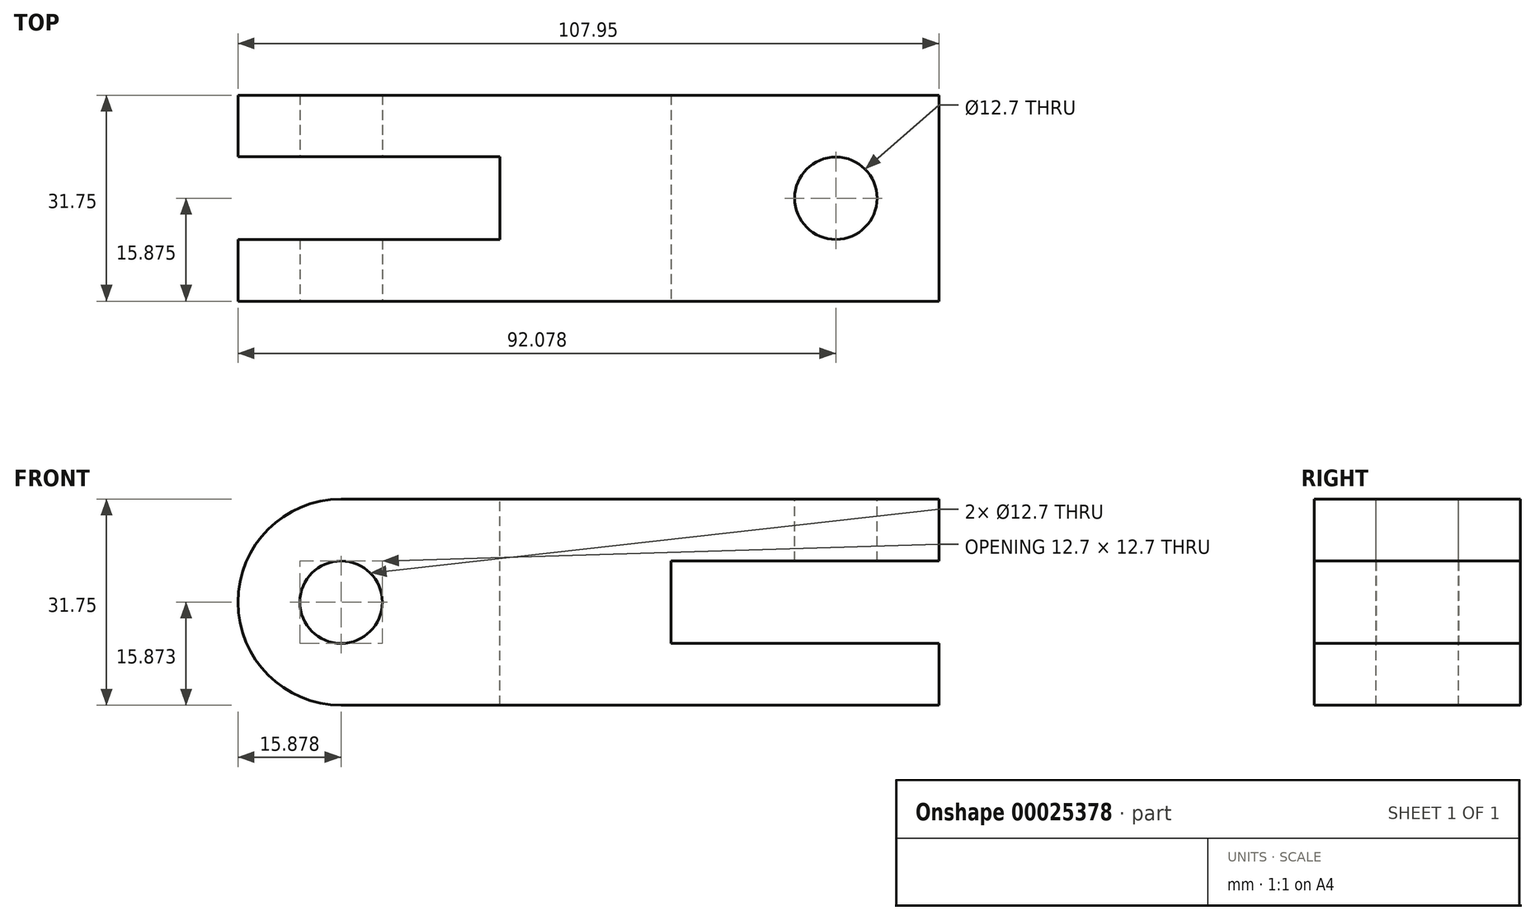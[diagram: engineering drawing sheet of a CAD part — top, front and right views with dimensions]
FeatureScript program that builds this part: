
annotation { "Feature Type Name" : "Feature", "Feature Type Description" : "" }
export const myFeature = defineFeature(function(context is Context, id is Id, definition is map)
    precondition{}
    {
        {
            var Q0;
            Q0=qCreatedBy(makeId("Front.planeOp"),FACE);
            var sketch = newSketch(context, id + "F0", { "sketchPlane" : qUnion([Q0])});
            skLineSegment(sketch, "E0.bottom", {"start": v(-0.97, -2.43) * mm, "end": v(106.98, -2.43) * mm});
            skLineSegment(sketch, "E0.top", {"start": v(-0.97, 29.32) * mm, "end": v(106.98, 29.32) * mm});
            skLineSegment(sketch, "E0.left", {"start": v(-0.97, -2.43) * mm, "end": v(-0.97, 29.32) * mm});
            skLineSegment(sketch, "E0.right", {"start": v(106.98, -2.43) * mm, "end": v(106.98, 29.32) * mm});
            skSolve(sketch);
        }
        {
            var Q0;
            Q0 = qSketchRegion(id + "F0", true);
            extrude(context, id + "F1", {"entities" : qUnion([Q0]), "depth" : 31.75 * mm});
        }
        {
            var Q0;
            Q0=makeQuery(id+"F1.opExtrude","CAP_FACE",FACE,{"disambiguationData":[OSD([sQuery(id+"F0.wireOp",EDGE,"E0.bottom"),sQuery(id+"F0.wireOp",EDGE,"E0.top"),sQuery(id+"F0.wireOp",EDGE,"E0.left"),sQuery(id+"F0.wireOp",EDGE,"E0.right")])],"isStart":false});
            var sketch = newSketch(context, id + "F2", { "sketchPlane" : qUnion([Q0])});
            skLineSegment(sketch, "E1.0", {"start": v(65.7, 7.1) * mm, "end": v(65.7, 19.8) * mm});
            skArc(sketch, "E2", {"start": v(14.9, 29.32) * mm, "mid": v(-0.97, 13.44) * mm, "end": v(14.9, -2.43) * mm});
            skCircle(sketch, "E3", {"center": v(14.9, 13.44) * mm, "radius": 6.35 * mm});
            skLineSegment(sketch, "E4.trimOffspring", {"start": v(65.7, 19.8) * mm, "end": v(106.98, 19.8) * mm});
            skLineSegment(sketch, "E5.trimOffspring", {"start": v(65.7, 7.1) * mm, "end": v(106.98, 7.1) * mm});
            skLineSegment(sketch, "E6", {"start": v(14.9, 13.44) * mm, "end": v(-0.97, 13.44) * mm, "construction": true});
            skSolve(sketch);
        }
        {
            var Q0;
            Q0 = qSketchRegion(id + "F2", true);
            var Q1;
            {var subQ1=sQuery(id+"F2.wireOp",EDGE,"E2");var subQ3=makeQuery(id+"F1.opExtrude","CAP_EDGE",EDGE,{"disambiguationData":[OSD([sQuery(id+"F0.wireOp",EDGE,"E0.top")])],"isStart":false});var subQ5=makeQuery(id+"F2.imprint","INTERSECT",VERTEX,{"derivedFrom":[subQ3,subQ1]});Q1=makeQuery(id+"F2.imprint","IMPRINT",FACE,{"disambiguationData":[TD([[makeQuery(id+"F2.imprint","IMPRINT",EDGE,{"disambiguationData":[TD([[subQ5,-1.0]])],"derivedFrom":subQ1}),-1.0]])]});}
            var Q2;
            {var subQ1=sQuery(id+"F2.wireOp",EDGE,"E2");var subQ3=makeQuery(id+"F1.opExtrude","CAP_EDGE",EDGE,{"disambiguationData":[OSD([sQuery(id+"F0.wireOp",EDGE,"E0.bottom")])],"isStart":false});var subQ5=makeQuery(id+"F2.imprint","INTERSECT",VERTEX,{"derivedFrom":[subQ3,subQ1]});Q2=makeQuery(id+"F2.imprint","IMPRINT",FACE,{"disambiguationData":[TD([[makeQuery(id+"F2.imprint","IMPRINT",EDGE,{"disambiguationData":[TD([[subQ5,1.0]])],"derivedFrom":subQ1}),-1.0]])]});}
            var Q3;
            Q3=makeQuery(id+"F2.imprint","IMPRINT",FACE,{"disambiguationData":[TD([[makeQuery(id+"F2.imprint","IMPRINT",EDGE,{"derivedFrom":sQuery(id+"F2.wireOp",EDGE,"E1.0")}),-1.0]])]});
            extrude(context, id + "F3", {"entities" : qUnion([Q0, Q1, Q2, Q3]), "operationType" : NewBodyOperationType.REMOVE, "endBound" : BoundingType.THROUGH_ALL, "oppositeDirection" : true, "depth" : 25.4 * mm});
        }
        {
            var Q0;
            Q0=makeQuery(id+"F1.opExtrude","SWEPT_FACE",FACE,{"disambiguationData":[OSD([sQuery(id+"F0.wireOp",EDGE,"E0.top")])]});
            var sketch = newSketch(context, id + "F4", { "sketchPlane" : qUnion([Q0])});
            skLineSegment(sketch, "E7", {"start": v(106.98, -15.88) * mm, "end": v(91.1, -15.88) * mm, "construction": true});
            skCircle(sketch, "E8", {"center": v(91.1, -15.88) * mm, "radius": 6.35 * mm});
            skLineSegment(sketch, "E9", {"start": v(14.9, 0) * mm, "end": v(14.9, -31.75) * mm, "construction": true});
            skLineSegment(sketch, "E10", {"start": v(14.9, -10.33) * mm, "end": v(14.9, -15.88) * mm, "construction": true});
            skLineSegment(sketch, "E11", {"start": v(14.9, -15.88) * mm, "end": v(106.98, -15.88) * mm, "construction": true});
            skLineSegment(sketch, "E12.top", {"start": v(14.9, -9.5) * mm, "end": v(39.35, -9.5) * mm});
            skLineSegment(sketch, "E12.left", {"start": v(14.9, -15.88) * mm, "end": v(14.9, -9.5) * mm});
            skLineSegment(sketch, "E12.right", {"start": v(39.35, -15.88) * mm, "end": v(39.35, -9.5) * mm});
            skLineSegment(sketch, "E13.bottom", {"start": v(14.9, -9.5) * mm, "end": v(-2.79, -9.5) * mm});
            skLineSegment(sketch, "E13.left", {"start": v(14.9, -9.5) * mm, "end": v(14.9, -10.33) * mm});
            skLineSegment(sketch, "E13.right", {"start": v(-2.79, -9.5) * mm, "end": v(-2.79, -15.88) * mm});
            skLineSegment(sketch, "E14.MirrorCS", {"start": v(14.9, -22.25) * mm, "end": v(39.35, -22.25) * mm});
            skLineSegment(sketch, "E15.MirrorCS", {"start": v(39.35, -15.88) * mm, "end": v(39.35, -22.25) * mm});
            skLineSegment(sketch, "E16.MirrorCS", {"start": v(14.9, -22.25) * mm, "end": v(-2.79, -22.25) * mm});
            skLineSegment(sketch, "E17.MirrorCS", {"start": v(-2.79, -22.25) * mm, "end": v(-2.79, -15.88) * mm});
            skSolve(sketch);
        }
        {
            var Q0;
            Q0 = qSketchRegion(id + "F4", true);
            var Q1;
            Q1=makeQuery(id+"F1.opExtrude","SWEPT_BODY",BODY,{"disambiguationData":[OSD([sQuery(id+"F0.wireOp",EDGE,"E0.bottom"),sQuery(id+"F0.wireOp",EDGE,"E0.top"),sQuery(id+"F0.wireOp",EDGE,"E0.left"),sQuery(id+"F0.wireOp",EDGE,"E0.right")])]});
            extrude(context, id + "F5", {"entities" : qUnion([Q0]), "operationType" : NewBodyOperationType.REMOVE, "endBound" : BoundingType.UP_TO_BODY, "oppositeDirection" : true, "endBoundEntityBody" : qUnion([Q1]), "depth" : 25.4 * mm});
        }
    });
